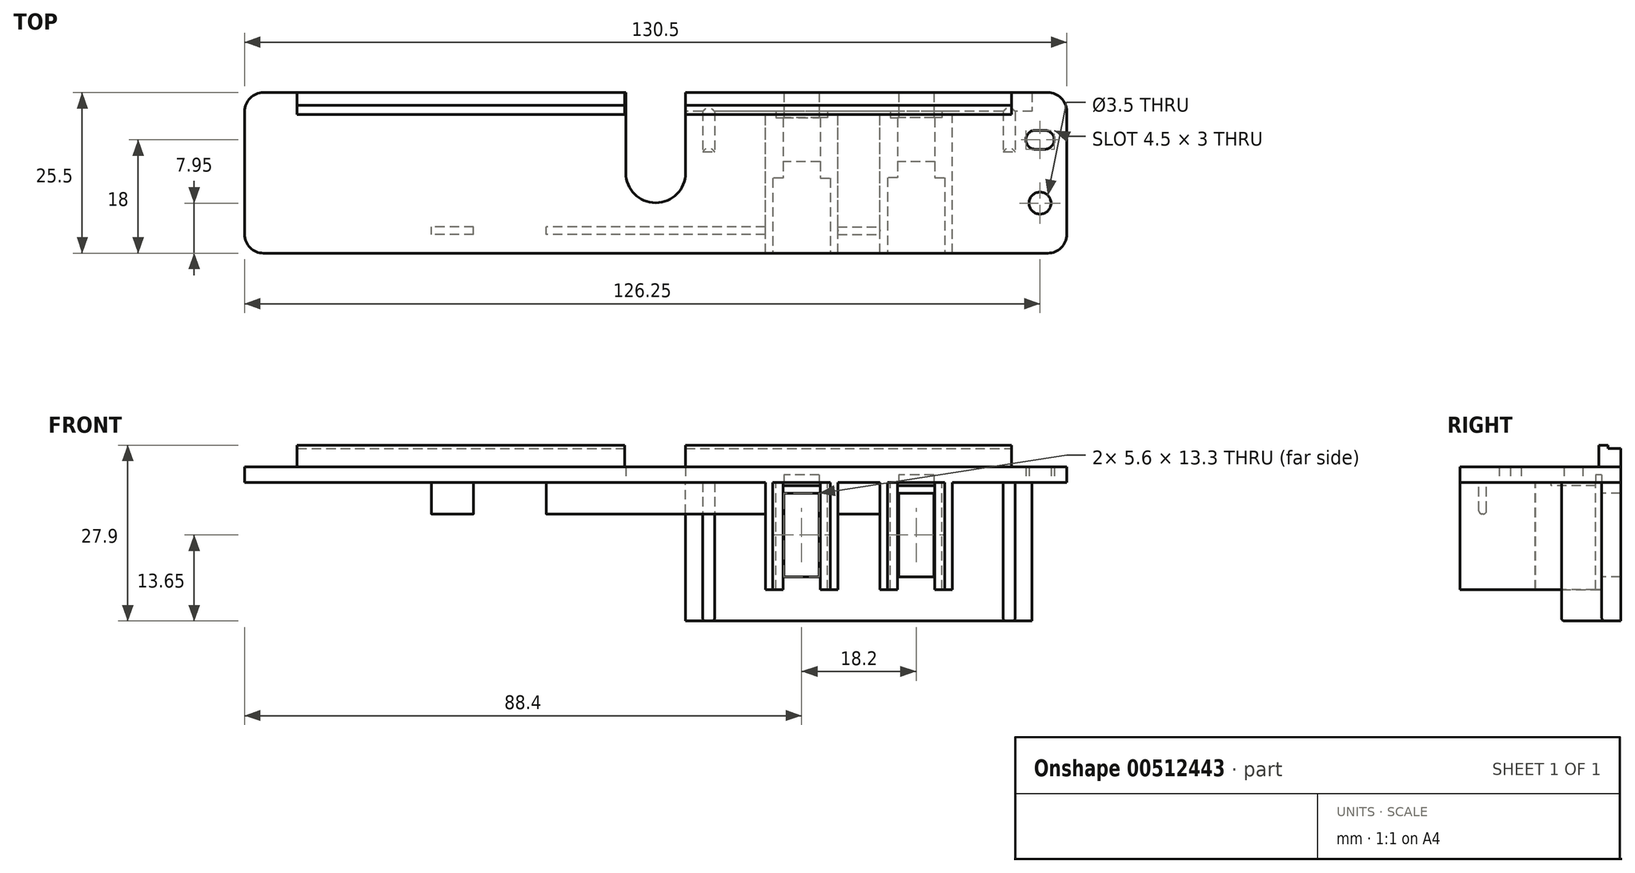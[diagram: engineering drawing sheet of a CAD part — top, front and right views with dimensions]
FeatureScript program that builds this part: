
annotation { "Feature Type Name" : "Feature", "Feature Type Description" : "" }
export const myFeature = defineFeature(function(context is Context, id is Id, definition is map)
    precondition{}
    {
        {
            var Q0;
            Q0=qCreatedBy(makeId("Top.planeOp"),FACE);
            var sketch = newSketch(context, id + "F0", { "sketchPlane" : qUnion([Q0])});
            skLineSegment(sketch, "E0.bottom", {"start": v(65.25, -12.75) * mm, "end": v(-65.25, -12.75) * mm});
            skLineSegment(sketch, "E0.top", {"start": v(65.25, 12.75) * mm, "end": v(-65.25, 12.75) * mm});
            skLineSegment(sketch, "E0.left", {"start": v(65.25, -12.75) * mm, "end": v(65.25, 12.75) * mm});
            skLineSegment(sketch, "E0.right", {"start": v(-65.25, -12.75) * mm, "end": v(-65.25, 12.75) * mm});
            skPoint(sketch, "E0.middle", {"position": v(0, 0) * mm});
            skSolve(sketch);
        }
        {
            var Q0;
            Q0=makeQuery(id+"F0.imprint","IMPRINT",FACE,{"disambiguationData":[TD([[makeQuery(id+"F0.imprint","IMPRINT",EDGE,{"derivedFrom":sQuery(id+"F0.wireOp",EDGE,"E0.bottom")}),-1.0]])]});
            extrude(context, id + "F1", {"entities" : qUnion([Q0]), "depth" : 2.5 * mm});
        }
        {
            var Q0;
            Q0=makeQuery(id+"F1.opExtrude","SWEPT_EDGE",EDGE,{"disambiguationData":[OSD([sQuery(id+"F0.wireOp",EDGE,"E0.top"),sQuery(id+"F0.wireOp",EDGE,"E0.right")])]});
            var Q1;
            Q1=makeQuery(id+"F1.opExtrude","SWEPT_EDGE",EDGE,{"disambiguationData":[OSD([sQuery(id+"F0.wireOp",EDGE,"E0.bottom"),sQuery(id+"F0.wireOp",EDGE,"E0.right")])]});
            var Q2;
            Q2=makeQuery(id+"F1.opExtrude","SWEPT_EDGE",EDGE,{"disambiguationData":[OSD([sQuery(id+"F0.wireOp",EDGE,"E0.top"),sQuery(id+"F0.wireOp",EDGE,"E0.left")])]});
            var Q3;
            Q3=makeQuery(id+"F1.opExtrude","SWEPT_EDGE",EDGE,{"disambiguationData":[OSD([sQuery(id+"F0.wireOp",EDGE,"E0.bottom"),sQuery(id+"F0.wireOp",EDGE,"E0.left")])]});
            fillet(context, id + "F2", {"entities" : qUnion([Q0, Q1, Q2, Q3]), "radius" : 3 * mm, "tangentPropagation" : true, "allowEdgeOverflow" : false});
        }
        {
            var Q0;
            Q0=makeQuery(id+"F1.opExtrude","CAP_FACE",FACE,{"disambiguationData":[OSD([sQuery(id+"F0.wireOp",EDGE,"E0.bottom"),sQuery(id+"F0.wireOp",EDGE,"E0.top"),sQuery(id+"F0.wireOp",EDGE,"E0.left"),sQuery(id+"F0.wireOp",EDGE,"E0.right")])],"isStart":false});
            var sketch = newSketch(context, id + "F3", { "sketchPlane" : qUnion([Q0])});
            skLineSegment(sketch, "E1.bottom", {"start": v(-56.9, 12.75) * mm, "end": v(-4.9, 12.75) * mm});
            skLineSegment(sketch, "E1.top", {"start": v(-56.9, 9.25) * mm, "end": v(-4.9, 9.25) * mm});
            skLineSegment(sketch, "E1.left", {"start": v(-56.9, 12.75) * mm, "end": v(-56.9, 9.25) * mm});
            skLineSegment(sketch, "E1.right", {"start": v(-4.9, 12.75) * mm, "end": v(-4.9, 9.25) * mm});
            skLineSegment(sketch, "E2.bottom", {"start": v(4.5, 12.75) * mm, "end": v(56.5, 12.75) * mm});
            skLineSegment(sketch, "E2.top", {"start": v(4.5, 9.25) * mm, "end": v(56.5, 9.25) * mm});
            skLineSegment(sketch, "E2.left", {"start": v(4.5, 12.75) * mm, "end": v(4.5, 9.25) * mm});
            skLineSegment(sketch, "E2.right", {"start": v(56.5, 12.75) * mm, "end": v(56.5, 9.25) * mm});
            skSolve(sketch);
        }
        {
            var Q0;
            Q0=makeQuery(id+"F3.imprint","IMPRINT",FACE,{"disambiguationData":[TD([[makeQuery(id+"F3.imprint","IMPRINT",EDGE,{"derivedFrom":sQuery(id+"F3.wireOp",EDGE,"E1.bottom")}),1.0]])]});
            var Q1;
            Q1=makeQuery(id+"F3.imprint","IMPRINT",FACE,{"disambiguationData":[TD([[makeQuery(id+"F3.imprint","IMPRINT",EDGE,{"derivedFrom":sQuery(id+"F3.wireOp",EDGE,"E2.bottom")}),1.0]])]});
            extrude(context, id + "F4", {"entities" : qUnion([Q0, Q1]), "operationType" : NewBodyOperationType.ADD, "depth" : 3.4 * mm, "offsetDistance" : 25 * mm});
        }
        {
            var Q0;
            Q0=makeQuery(id+"F1.opExtrude","CAP_FACE",FACE,{"disambiguationData":[OSD([sQuery(id+"F0.wireOp",EDGE,"E0.bottom"),sQuery(id+"F0.wireOp",EDGE,"E0.top"),sQuery(id+"F0.wireOp",EDGE,"E0.left"),sQuery(id+"F0.wireOp",EDGE,"E0.right")])],"isStart":true});
            var sketch = newSketch(context, id + "F5", { "sketchPlane" : qUnion([Q0])});
            skLineSegment(sketch, "E3.bottom", {"start": v(59.75, -12.75) * mm, "end": v(4.75, -12.75) * mm});
            skLineSegment(sketch, "E3.top", {"start": v(59.75, -9.75) * mm, "end": v(4.75, -9.75) * mm});
            skLineSegment(sketch, "E3.left", {"start": v(59.75, -12.75) * mm, "end": v(59.75, -9.75) * mm});
            skLineSegment(sketch, "E3.right", {"start": v(4.75, -12.75) * mm, "end": v(4.75, -9.75) * mm});
            skSolve(sketch);
        }
        {
            var Q0;
            Q0=makeQuery(id+"F5.imprint","IMPRINT",FACE,{"disambiguationData":[TD([[makeQuery(id+"F5.imprint","IMPRINT",EDGE,{"derivedFrom":sQuery(id+"F5.wireOp",EDGE,"E3.bottom")}),-1.0]])]});
            extrude(context, id + "F6", {"entities" : qUnion([Q0]), "operationType" : NewBodyOperationType.ADD, "depth" : 22 * mm, "offsetDistance" : 25 * mm});
        }
        {
            var Q0;
            Q0=makeQuery(id+"F6.opExtrude","CAP_FACE",FACE,{"disambiguationData":[OSD([sQuery(id+"F5.wireOp",EDGE,"E3.bottom"),sQuery(id+"F5.wireOp",EDGE,"E3.top"),sQuery(id+"F5.wireOp",EDGE,"E3.left"),sQuery(id+"F5.wireOp",EDGE,"E3.right")])],"isStart":false});
            var sketch = newSketch(context, id + "F7", { "sketchPlane" : qUnion([Q0])});
            skLineSegment(sketch, "E4.bottom", {"start": v(55.15, -9.75) * mm, "end": v(57.05, -9.75) * mm});
            skLineSegment(sketch, "E4.top", {"start": v(55.15, -3.35) * mm, "end": v(57.05, -3.35) * mm});
            skLineSegment(sketch, "E4.left", {"start": v(55.15, -9.75) * mm, "end": v(55.15, -3.35) * mm});
            skLineSegment(sketch, "E4.right", {"start": v(57.05, -9.75) * mm, "end": v(57.05, -3.35) * mm});
            skSolve(sketch);
        }
        {
            var Q0;
            Q0=makeQuery(id+"F7.imprint","IMPRINT",FACE,{"disambiguationData":[TD([[makeQuery(id+"F7.imprint","IMPRINT",EDGE,{"derivedFrom":sQuery(id+"F7.wireOp",EDGE,"E4.bottom")}),-1.0]])]});
            extrude(context, id + "F8", {"entities" : qUnion([Q0]), "operationType" : NewBodyOperationType.ADD, "endBound" : BoundingType.UP_TO_NEXT, "oppositeDirection" : true, "depth" : 25 * mm, "offsetDistance" : 25 * mm});
        }
        {
            var Q0;
            Q0=makeQuery(id+"F8.boolean.opBoolean","MERGE",FACE,{"derivedFrom":[makeQuery(id+"F6.opExtrude","CAP_FACE",FACE,{"disambiguationData":[OSD([sQuery(id+"F5.wireOp",EDGE,"E3.bottom"),sQuery(id+"F5.wireOp",EDGE,"E3.top"),sQuery(id+"F5.wireOp",EDGE,"E3.left"),sQuery(id+"F5.wireOp",EDGE,"E3.right")])],"isStart":false}),makeQuery(id+"F8.opExtrude","CAP_FACE",FACE,{"disambiguationData":[OSD([sQuery(id+"F7.wireOp",EDGE,"E4.bottom"),sQuery(id+"F7.wireOp",EDGE,"E4.top"),sQuery(id+"F7.wireOp",EDGE,"E4.left"),sQuery(id+"F7.wireOp",EDGE,"E4.right")])],"isStart":true})]});
            var sketch = newSketch(context, id + "F9", { "sketchPlane" : qUnion([Q0])});
            skLineSegment(sketch, "E5.bottom", {"start": v(7.45, -9.75) * mm, "end": v(9.35, -9.75) * mm});
            skLineSegment(sketch, "E5.top", {"start": v(7.45, -3.35) * mm, "end": v(9.35, -3.35) * mm});
            skLineSegment(sketch, "E5.left", {"start": v(7.45, -9.75) * mm, "end": v(7.45, -3.35) * mm});
            skLineSegment(sketch, "E5.right", {"start": v(9.35, -9.75) * mm, "end": v(9.35, -3.35) * mm});
            skSolve(sketch);
        }
        {
            var Q0;
            Q0=makeQuery(id+"F9.imprint","IMPRINT",FACE,{"disambiguationData":[TD([[makeQuery(id+"F9.imprint","IMPRINT",EDGE,{"derivedFrom":sQuery(id+"F9.wireOp",EDGE,"E5.bottom")}),-1.0]])]});
            extrude(context, id + "F10", {"entities" : qUnion([Q0]), "operationType" : NewBodyOperationType.ADD, "endBound" : BoundingType.UP_TO_NEXT, "oppositeDirection" : true, "depth" : 25 * mm, "offsetDistance" : 25 * mm});
        }
        {
            var Q0;
            {var subQ0=sQuery(id+"F0.wireOp",EDGE,"E0.bottom");var subQ1=sQuery(id+"F0.wireOp",EDGE,"E0.left");var subQ2=sQuery(id+"F0.wireOp",EDGE,"E0.top");Q0=makeQuery(id+"FTl0xKzHUKMtFWp_1.boolean.opBoolean","SPLIT",FACE,{"disambiguationData":[TD([makeQuery(id+"F1.opExtrude","SWEPT_FACE",FACE,{"disambiguationData":[OSD([subQ1])]})])],"derivedFrom":makeQuery(id+"F1.opExtrude","CAP_FACE",FACE,{"disambiguationData":[OSD([subQ0,subQ2,subQ1,sQuery(id+"F0.wireOp",EDGE,"E0.right")])],"isStart":true})});}
            var sketch = newSketch(context, id + "F11", { "sketchPlane" : qUnion([Q0])});
            skCircle(sketch, "E6", {"center": v(61, 4.8) * mm, "radius": 1.75 * mm});
            skSolve(sketch);
        }
        {
            var Q0;
            Q0=makeQuery(id+"F11.imprint","IMPRINT",FACE,{"disambiguationData":[TD([[makeQuery(id+"F11.imprint","IMPRINT",EDGE,{"derivedFrom":sQuery(id+"F11.wireOp",EDGE,"E6")}),1.0]])]});
            extrude(context, id + "F12", {"entities" : qUnion([Q0]), "operationType" : NewBodyOperationType.REMOVE, "endBound" : BoundingType.UP_TO_NEXT, "oppositeDirection" : true, "depth" : 25 * mm, "offsetDistance" : 25 * mm});
        }
        {
            var Q0;
            {var subQ0=sQuery(id+"F0.wireOp",EDGE,"E0.bottom");var subQ1=sQuery(id+"F0.wireOp",EDGE,"E0.left");var subQ2=sQuery(id+"F0.wireOp",EDGE,"E0.top");Q0=makeQuery(id+"FTl0xKzHUKMtFWp_1.boolean.opBoolean","SPLIT",FACE,{"disambiguationData":[TD([makeQuery(id+"F1.opExtrude","SWEPT_FACE",FACE,{"disambiguationData":[OSD([subQ1])]})])],"derivedFrom":makeQuery(id+"F1.opExtrude","CAP_FACE",FACE,{"disambiguationData":[OSD([subQ0,subQ2,subQ1,sQuery(id+"F0.wireOp",EDGE,"E0.right")])],"isStart":true})});}
            var sketch = newSketch(context, id + "F13", { "sketchPlane" : qUnion([Q0])});
            skLineSegment(sketch, "E7.bottom", {"start": v(60.25, -3.75) * mm, "end": v(61.75, -3.75) * mm});
            skLineSegment(sketch, "E7.top", {"start": v(60.25, -6.75) * mm, "end": v(61.75, -6.75) * mm});
            skLineSegment(sketch, "E7.left", {"start": v(58.75, -5.25) * mm, "end": v(58.75, -5.25) * mm});
            skLineSegment(sketch, "E7.right", {"start": v(63.25, -5.25) * mm, "end": v(63.25, -5.25) * mm});
            skPoint(sketch, "E8.visualSharp", {"position": v(58.75, -3.75) * mm});
            skArc(sketch, "E8.filletArc", {"start": v(60.25, -3.75) * mm, "mid": v(59.19, -4.19) * mm, "end": v(58.75, -5.25) * mm});
            skPoint(sketch, "E9.visualSharp", {"position": v(58.75, -6.75) * mm});
            skArc(sketch, "E9.filletArc", {"start": v(58.75, -5.25) * mm, "mid": v(59.19, -6.31) * mm, "end": v(60.25, -6.75) * mm});
            skPoint(sketch, "E10.visualSharp", {"position": v(63.25, -6.75) * mm});
            skArc(sketch, "E10.filletArc", {"start": v(61.75, -6.75) * mm, "mid": v(62.81, -6.31) * mm, "end": v(63.25, -5.25) * mm});
            skPoint(sketch, "E11.visualSharp", {"position": v(63.25, -3.75) * mm});
            skArc(sketch, "E11.filletArc", {"start": v(63.25, -5.25) * mm, "mid": v(62.81, -4.19) * mm, "end": v(61.75, -3.75) * mm});
            skSolve(sketch);
        }
        {
            var Q0;
            Q0=makeQuery(id+"F13.imprint","IMPRINT",FACE,{"disambiguationData":[TD([[makeQuery(id+"F13.imprint","IMPRINT",EDGE,{"derivedFrom":sQuery(id+"F13.wireOp",EDGE,"E7.bottom")}),-1.0]])]});
            extrude(context, id + "F14", {"entities" : qUnion([Q0]), "operationType" : NewBodyOperationType.REMOVE, "endBound" : BoundingType.UP_TO_NEXT, "oppositeDirection" : true, "depth" : 25 * mm, "offsetDistance" : 25 * mm});
        }
        {
            var Q0;
            Q0=makeQuery(id+"F4.opExtrude","SWEPT_FACE",FACE,{"disambiguationData":[OSD([sQuery(id+"F3.wireOp",EDGE,"E2.right")])]});
            var sketch = newSketch(context, id + "F15", { "sketchPlane" : qUnion([Q0])});
            skLineSegment(sketch, "E12.bottom", {"start": v(12.75, 5.9) * mm, "end": v(10.75, 5.9) * mm});
            skLineSegment(sketch, "E12.top", {"start": v(12.75, 5.4) * mm, "end": v(10.75, 5.4) * mm});
            skLineSegment(sketch, "E12.left", {"start": v(12.75, 5.9) * mm, "end": v(12.75, 5.4) * mm});
            skLineSegment(sketch, "E12.right", {"start": v(10.75, 5.9) * mm, "end": v(10.75, 5.4) * mm});
            skSolve(sketch);
        }
        {
            var Q0;
            Q0=makeQuery(id+"F15.imprint","IMPRINT",FACE,{"disambiguationData":[TD([[makeQuery(id+"F15.imprint","IMPRINT",EDGE,{"derivedFrom":sQuery(id+"F15.wireOp",EDGE,"E12.bottom")}),1.0]])]});
            extrude(context, id + "F16", {"entities" : qUnion([Q0]), "operationType" : NewBodyOperationType.REMOVE, "endBound" : BoundingType.THROUGH_ALL, "oppositeDirection" : true, "depth" : 25 * mm, "offsetDistance" : 25 * mm});
        }
        {
            var Q0;
            {var subQ0=sQuery(id+"F7.wireOp",EDGE,"E4.left");var subQ2=sQuery(id+"F5.wireOp",EDGE,"E3.right");var subQ3=sQuery(id+"F5.wireOp",EDGE,"E3.top");var subQ6=makeQuery(id+"F8.opExtrude","SWEPT_FACE",FACE,{"disambiguationData":[OSD([subQ0])]});Q0=makeQuery(id+"F10.boolean.opBoolean","SPLIT",FACE,{"disambiguationData":[TD([subQ6])],"derivedFrom":makeQuery(id+"F8.boolean.opBoolean","SPLIT",FACE,{"disambiguationData":[TD([makeQuery(id+"F6.opExtrude","SWEPT_FACE",FACE,{"disambiguationData":[OSD([subQ2])]})])],"derivedFrom":makeQuery(id+"F6.opExtrude","SWEPT_FACE",FACE,{"disambiguationData":[OSD([subQ3])]})})});}
            var sketch = newSketch(context, id + "F17", { "sketchPlane" : qUnion([Q0])});
            skLineSegment(sketch, "E13.bottom", {"start": v(44.15, -1.7) * mm, "end": v(38.55, -1.7) * mm});
            skLineSegment(sketch, "E13.top", {"start": v(44.15, -15) * mm, "end": v(38.55, -15) * mm});
            skLineSegment(sketch, "E13.left", {"start": v(44.15, -1.7) * mm, "end": v(44.15, -15) * mm});
            skLineSegment(sketch, "E13.right", {"start": v(38.55, -1.7) * mm, "end": v(38.55, -15) * mm});
            skLineSegment(sketch, "E14.bottom", {"start": v(25.95, -1.7) * mm, "end": v(20.35, -1.7) * mm});
            skLineSegment(sketch, "E14.top", {"start": v(25.95, -15) * mm, "end": v(20.35, -15) * mm});
            skLineSegment(sketch, "E14.left", {"start": v(25.95, -1.7) * mm, "end": v(25.95, -15) * mm});
            skLineSegment(sketch, "E14.right", {"start": v(20.35, -1.7) * mm, "end": v(20.35, -15) * mm});
            skSolve(sketch);
        }
        {
            var Q0;
            Q0=makeQuery(id+"F17.imprint","IMPRINT",FACE,{"disambiguationData":[TD([[makeQuery(id+"F17.imprint","IMPRINT",EDGE,{"derivedFrom":sQuery(id+"F17.wireOp",EDGE,"E13.bottom")}),1.0]])]});
            var Q1;
            Q1=makeQuery(id+"F17.imprint","IMPRINT",FACE,{"disambiguationData":[TD([[makeQuery(id+"F17.imprint","IMPRINT",EDGE,{"derivedFrom":sQuery(id+"F17.wireOp",EDGE,"E14.bottom")}),1.0]])]});
            extrude(context, id + "F18", {"entities" : qUnion([Q0, Q1]), "operationType" : NewBodyOperationType.REMOVE, "endBound" : BoundingType.THROUGH_ALL, "oppositeDirection" : true, "depth" : 25 * mm, "offsetDistance" : 25 * mm});
        }
        {
            var Q0;
            Q0=makeQuery(id+"F1.opExtrude","CAP_FACE",FACE,{"disambiguationData":[OSD([sQuery(id+"F0.wireOp",EDGE,"E0.bottom"),sQuery(id+"F0.wireOp",EDGE,"E0.top"),sQuery(id+"F0.wireOp",EDGE,"E0.left"),sQuery(id+"F0.wireOp",EDGE,"E0.right")])],"isStart":true});
            var sketch = newSketch(context, id + "F19", { "sketchPlane" : qUnion([Q0])});
            skLineSegment(sketch, "E15.bottom", {"start": v(44.15, -9.75) * mm, "end": v(38.55, -9.75) * mm});
            skLineSegment(sketch, "E15.top", {"start": v(44.15, -8.75) * mm, "end": v(38.55, -8.75) * mm});
            skLineSegment(sketch, "E15.left", {"start": v(44.15, -9.75) * mm, "end": v(44.15, -8.75) * mm});
            skLineSegment(sketch, "E15.right", {"start": v(38.55, -9.75) * mm, "end": v(38.55, -8.75) * mm});
            skLineSegment(sketch, "E16.bottom", {"start": v(20.35, -9.75) * mm, "end": v(25.95, -9.75) * mm});
            skLineSegment(sketch, "E16.top", {"start": v(20.35, -8.75) * mm, "end": v(25.95, -8.75) * mm});
            skLineSegment(sketch, "E16.left", {"start": v(20.35, -9.75) * mm, "end": v(20.35, -8.75) * mm});
            skLineSegment(sketch, "E16.right", {"start": v(25.95, -9.75) * mm, "end": v(25.95, -8.75) * mm});
            skSolve(sketch);
        }
        {
            var Q0;
            Q0=makeQuery(id+"F19.imprint","IMPRINT",FACE,{"disambiguationData":[TD([[makeQuery(id+"F19.imprint","IMPRINT",EDGE,{"derivedFrom":sQuery(id+"F19.wireOp",EDGE,"E15.bottom")}),-1.0]])]});
            var Q1;
            Q1=makeQuery(id+"F19.imprint","IMPRINT",FACE,{"disambiguationData":[TD([[makeQuery(id+"F19.imprint","IMPRINT",EDGE,{"derivedFrom":sQuery(id+"F19.wireOp",EDGE,"E16.bottom")}),-1.0]])]});
            extrude(context, id + "F20", {"entities" : qUnion([Q0, Q1]), "operationType" : NewBodyOperationType.REMOVE, "oppositeDirection" : true, "depth" : 1.2 * mm, "offsetDistance" : 25 * mm});
        }
        {
            var Q0;
            Q0=makeQuery(id+"F1.opExtrude","CAP_FACE",FACE,{"disambiguationData":[OSD([sQuery(id+"F0.wireOp",EDGE,"E0.bottom"),sQuery(id+"F0.wireOp",EDGE,"E0.top"),sQuery(id+"F0.wireOp",EDGE,"E0.left"),sQuery(id+"F0.wireOp",EDGE,"E0.right")])],"isStart":true});
            var sketch = newSketch(context, id + "F21", { "sketchPlane" : qUnion([Q0])});
            skLineSegment(sketch, "E17", {"start": v(45.45, -9.75) * mm, "end": v(45.45, -8.75) * mm});
            skLineSegment(sketch, "E18", {"start": v(45.45, -8.75) * mm, "end": v(44.3, -8.75) * mm});
            skLineSegment(sketch, "E19", {"start": v(44.3, -8.75) * mm, "end": v(44.3, 0.75) * mm});
            skLineSegment(sketch, "E20", {"start": v(44.3, 0.75) * mm, "end": v(45.9, 0.75) * mm});
            skLineSegment(sketch, "E21", {"start": v(45.9, 0.75) * mm, "end": v(45.9, 12.75) * mm});
            skLineSegment(sketch, "E22", {"start": v(45.9, 12.75) * mm, "end": v(47.1, 12.75) * mm});
            skLineSegment(sketch, "E23", {"start": v(47.1, 12.75) * mm, "end": v(47.1, -9.75) * mm});
            skLineSegment(sketch, "E24", {"start": v(47.1, -9.75) * mm, "end": v(45.45, -9.75) * mm});
            skLineSegment(sketch, "E25", {"start": v(37.25, -9.75) * mm, "end": v(37.25, -8.75) * mm});
            skLineSegment(sketch, "E26", {"start": v(37.25, -8.75) * mm, "end": v(38.4, -8.75) * mm});
            skLineSegment(sketch, "E27", {"start": v(38.4, -8.75) * mm, "end": v(38.4, 0.75) * mm});
            skLineSegment(sketch, "E28", {"start": v(38.4, 0.75) * mm, "end": v(36.8, 0.75) * mm});
            skLineSegment(sketch, "E29", {"start": v(36.8, 0.75) * mm, "end": v(36.8, 12.75) * mm});
            skLineSegment(sketch, "E30", {"start": v(36.8, 12.75) * mm, "end": v(35.6, 12.75) * mm});
            skLineSegment(sketch, "E31", {"start": v(35.6, 12.75) * mm, "end": v(35.6, -9.75) * mm});
            skLineSegment(sketch, "E32", {"start": v(35.6, -9.75) * mm, "end": v(37.25, -9.75) * mm});
            skLineSegment(sketch, "E33", {"start": v(28.9, 12.75) * mm, "end": v(28.9, -9.75) * mm});
            skLineSegment(sketch, "E34", {"start": v(28.9, -9.75) * mm, "end": v(27.25, -9.75) * mm});
            skLineSegment(sketch, "E35", {"start": v(27.25, -9.75) * mm, "end": v(27.25, -8.75) * mm});
            skLineSegment(sketch, "E36", {"start": v(27.25, -8.75) * mm, "end": v(26.1, -8.75) * mm});
            skLineSegment(sketch, "E37", {"start": v(26.1, -8.75) * mm, "end": v(26.1, 0.85) * mm});
            skLineSegment(sketch, "E38", {"start": v(26.1, 0.85) * mm, "end": v(27.7, 0.85) * mm});
            skLineSegment(sketch, "E39", {"start": v(27.7, 0.85) * mm, "end": v(27.7, 12.75) * mm});
            skLineSegment(sketch, "E40", {"start": v(27.7, 12.75) * mm, "end": v(28.9, 12.75) * mm});
            skLineSegment(sketch, "E41", {"start": v(19.05, -9.75) * mm, "end": v(19.05, -8.75) * mm});
            skLineSegment(sketch, "E42", {"start": v(19.05, -8.75) * mm, "end": v(20.2, -8.75) * mm});
            skLineSegment(sketch, "E43", {"start": v(20.2, -8.75) * mm, "end": v(20.2, 0.85) * mm});
            skLineSegment(sketch, "E44", {"start": v(20.2, 0.85) * mm, "end": v(18.6, 0.85) * mm});
            skLineSegment(sketch, "E45", {"start": v(18.6, 0.85) * mm, "end": v(18.6, 12.75) * mm});
            skLineSegment(sketch, "E46", {"start": v(18.6, 12.75) * mm, "end": v(17.4, 12.75) * mm});
            skLineSegment(sketch, "E47", {"start": v(17.4, 12.75) * mm, "end": v(17.4, -9.75) * mm});
            skLineSegment(sketch, "E48", {"start": v(17.4, -9.75) * mm, "end": v(19.05, -9.75) * mm});
            skSolve(sketch);
        }
        {
            var Q0;
            Q0=makeQuery(id+"F21.imprint","IMPRINT",FACE,{"disambiguationData":[TD([[makeQuery(id+"F21.imprint","IMPRINT",EDGE,{"derivedFrom":sQuery(id+"F21.wireOp",EDGE,"E17")}),-1.0]])]});
            var Q1;
            Q1=makeQuery(id+"F21.imprint","IMPRINT",FACE,{"disambiguationData":[TD([[makeQuery(id+"F21.imprint","IMPRINT",EDGE,{"derivedFrom":sQuery(id+"F21.wireOp",EDGE,"E25")}),1.0]])]});
            var Q2;
            Q2=makeQuery(id+"F21.imprint","IMPRINT",FACE,{"disambiguationData":[TD([[makeQuery(id+"F21.imprint","IMPRINT",EDGE,{"derivedFrom":sQuery(id+"F21.wireOp",EDGE,"E33")}),-1.0]])]});
            var Q3;
            Q3=makeQuery(id+"F21.imprint","IMPRINT",FACE,{"disambiguationData":[TD([[makeQuery(id+"F21.imprint","IMPRINT",EDGE,{"derivedFrom":sQuery(id+"F21.wireOp",EDGE,"E41")}),1.0]])]});
            extrude(context, id + "F22", {"entities" : qUnion([Q0, Q1, Q2, Q3]), "operationType" : NewBodyOperationType.ADD, "depth" : 17 * mm, "offsetDistance" : 25 * mm});
        }
        {
            var Q0;
            {var subQ12=sQuery(id+"F5.wireOp",EDGE,"E3.top");var subQ25=sQuery(id+"F0.wireOp",EDGE,"E0.bottom");var subQ27=sQuery(id+"F0.wireOp",EDGE,"E0.top");var subQ35=makeQuery(id+"F6.opExtrude","SWEPT_FACE",FACE,{"disambiguationData":[OSD([subQ12])]});var subQ38=sQuery(id+"F0.wireOp",EDGE,"E0.right");Q0=makeQuery(id+"F36xmBUTzq5bmo9_1.1.F22.boolean.opBoolean","SPLIT",FACE,{"disambiguationData":[TD([subQ35])],"derivedFrom":makeQuery(id+"F22.boolean.opBoolean","SPLIT",FACE,{"disambiguationData":[TD([makeQuery(id+"F1.opExtrude","SWEPT_FACE",FACE,{"disambiguationData":[OSD([subQ38])]})])],"derivedFrom":makeQuery(id+"F1.opExtrude","CAP_FACE",FACE,{"disambiguationData":[OSD([subQ25,subQ27,sQuery(id+"F0.wireOp",EDGE,"E0.left"),subQ38])],"isStart":true})})});}
            var sketch = newSketch(context, id + "F23", { "sketchPlane" : qUnion([Q0])});
            skLineSegment(sketch, "E49.bottom", {"start": v(-4.75, -12.75) * mm, "end": v(4.75, -12.75) * mm});
            skLineSegment(sketch, "E49.top", {"start": v(-4.75, 0) * mm, "end": v(4.75, 0) * mm});
            skLineSegment(sketch, "E49.left", {"start": v(-4.75, -12.75) * mm, "end": v(-4.75, 0) * mm});
            skLineSegment(sketch, "E49.right", {"start": v(4.75, -12.75) * mm, "end": v(4.75, 0) * mm});
            skCircle(sketch, "E50", {"center": v(0, 0) * mm, "radius": 4.75 * mm});
            skSolve(sketch);
        }
        {
            var Q0;
            {var subQ0=sQuery(id+"F23.wireOp",EDGE,"E49.top");Q0=makeQuery(id+"F23.imprint","IMPRINT",FACE,{"disambiguationData":[TD([[makeQuery(id+"F23.imprint","IMPRINT",EDGE,{"derivedFrom":subQ0}),1.0]])]});}
            var Q1;
            {var subQ0=sQuery(id+"F23.wireOp",EDGE,"E49.top");Q1=makeQuery(id+"F23.imprint","IMPRINT",FACE,{"disambiguationData":[TD([[makeQuery(id+"F23.imprint","IMPRINT",EDGE,{"derivedFrom":subQ0}),-1.0]])]});}
            var Q2;
            {var subQ13=sQuery(id+"F23.wireOp",EDGE,"E49.bottom");Q2=makeQuery(id+"F23.imprint","IMPRINT",FACE,{"disambiguationData":[TD([[makeQuery(id+"F23.imprint","IMPRINT",EDGE,{"derivedFrom":subQ13}),-1.0]])]});}
            extrude(context, id + "F24", {"entities" : qUnion([Q0, Q1, Q2]), "operationType" : NewBodyOperationType.REMOVE, "endBound" : BoundingType.THROUGH_ALL, "oppositeDirection" : true, "depth" : 25 * mm, "offsetDistance" : 25 * mm});
        }
        {
            var Q0;
            {var subQ12=sQuery(id+"F5.wireOp",EDGE,"E3.top");var subQ25=sQuery(id+"F0.wireOp",EDGE,"E0.bottom");var subQ27=sQuery(id+"F0.wireOp",EDGE,"E0.top");var subQ35=makeQuery(id+"F6.opExtrude","SWEPT_FACE",FACE,{"disambiguationData":[OSD([subQ12])]});var subQ38=sQuery(id+"F0.wireOp",EDGE,"E0.right");Q0=makeQuery(id+"F36xmBUTzq5bmo9_1.1.F22.boolean.opBoolean","SPLIT",FACE,{"disambiguationData":[TD([subQ35])],"derivedFrom":makeQuery(id+"F22.boolean.opBoolean","SPLIT",FACE,{"disambiguationData":[TD([makeQuery(id+"F1.opExtrude","SWEPT_FACE",FACE,{"disambiguationData":[OSD([subQ38])]})])],"derivedFrom":makeQuery(id+"F1.opExtrude","CAP_FACE",FACE,{"disambiguationData":[OSD([subQ25,subQ27,sQuery(id+"F0.wireOp",EDGE,"E0.left"),subQ38])],"isStart":true})})});}
            var sketch = newSketch(context, id + "F25", { "sketchPlane" : qUnion([Q0])});
            skLineSegment(sketch, "E51.bottom", {"start": v(17.4, 9.75) * mm, "end": v(-17.4, 9.75) * mm});
            skLineSegment(sketch, "E51.top", {"start": v(17.4, 8.55) * mm, "end": v(-17.4, 8.55) * mm});
            skLineSegment(sketch, "E51.left", {"start": v(17.4, 9.75) * mm, "end": v(17.4, 8.55) * mm});
            skLineSegment(sketch, "E51.right", {"start": v(-17.4, 9.75) * mm, "end": v(-17.4, 8.55) * mm});
            skLineSegment(sketch, "E52.bottom", {"start": v(28.9, 8.55) * mm, "end": v(35.6, 8.55) * mm});
            skLineSegment(sketch, "E52.top", {"start": v(28.9, 9.75) * mm, "end": v(35.6, 9.75) * mm});
            skLineSegment(sketch, "E52.left", {"start": v(28.9, 8.55) * mm, "end": v(28.9, 9.75) * mm});
            skLineSegment(sketch, "E52.right", {"start": v(35.6, 8.55) * mm, "end": v(35.6, 9.75) * mm});
            skLineSegment(sketch, "E53.bottom", {"start": v(-28.9, 9.75) * mm, "end": v(-35.6, 9.75) * mm});
            skLineSegment(sketch, "E53.top", {"start": v(-28.9, 8.55) * mm, "end": v(-35.6, 8.55) * mm});
            skLineSegment(sketch, "E53.left", {"start": v(-28.9, 9.75) * mm, "end": v(-28.9, 8.55) * mm});
            skLineSegment(sketch, "E53.right", {"start": v(-35.6, 9.75) * mm, "end": v(-35.6, 8.55) * mm});
            skSolve(sketch);
        }
        {
            var Q0;
            Q0=makeQuery(id+"F25.imprint","IMPRINT",FACE,{"disambiguationData":[TD([[makeQuery(id+"F25.imprint","IMPRINT",EDGE,{"derivedFrom":sQuery(id+"F25.wireOp",EDGE,"E52.bottom")}),1.0]])]});
            var Q1;
            Q1=makeQuery(id+"F25.imprint","IMPRINT",FACE,{"disambiguationData":[TD([[makeQuery(id+"F25.imprint","IMPRINT",EDGE,{"derivedFrom":sQuery(id+"F25.wireOp",EDGE,"E51.bottom")}),1.0]])]});
            var Q2;
            Q2=makeQuery(id+"F25.imprint","IMPRINT",FACE,{"disambiguationData":[TD([[makeQuery(id+"F25.imprint","IMPRINT",EDGE,{"derivedFrom":sQuery(id+"F25.wireOp",EDGE,"E53.bottom")}),1.0]])]});
            extrude(context, id + "F26", {"entities" : qUnion([Q0, Q1, Q2]), "operationType" : NewBodyOperationType.ADD, "depth" : 5 * mm, "offsetDistance" : 25 * mm});
        }
        {
            var Q0;
            {var subQ0=sQuery(id+"F7.wireOp",EDGE,"E4.left");var subQ2=makeQuery(id+"F8.opExtrude","SWEPT_FACE",FACE,{"disambiguationData":[OSD([subQ0])]});var subQ3=sQuery(id+"F5.wireOp",EDGE,"E3.top");var subQ5=sQuery(id+"F5.wireOp",EDGE,"E3.right");Q0=makeQuery(id+"F10.boolean.opBoolean","SPLIT",EDGE,{"disambiguationData":[TD([subQ2])],"derivedFrom":makeQuery(id+"F8.boolean.opBoolean","SPLIT",EDGE,{"disambiguationData":[TD([makeQuery(id+"F6.opExtrude","SWEPT_FACE",FACE,{"disambiguationData":[OSD([subQ5])]})])],"derivedFrom":makeQuery(id+"F6.opExtrude","CAP_EDGE",EDGE,{"disambiguationData":[OSD([subQ3])],"isStart":false})})});}
            var Q1;
            {var subQ0=sQuery(id+"F7.wireOp",EDGE,"E4.left");var subQ1=makeQuery(id+"FbdN5aHEnnnu9Vr_1.1.F8.opExtrude","SWEPT_FACE",FACE,{"disambiguationData":[OSD([subQ0])]});var subQ4=sQuery(id+"F5.wireOp",EDGE,"E3.top");var subQ6=sQuery(id+"F5.wireOp",EDGE,"E3.right");Q1=makeQuery(id+"FbdN5aHEnnnu9Vr_1.1.F10.boolean.opBoolean","SPLIT",EDGE,{"disambiguationData":[TD([subQ1])],"derivedFrom":makeQuery(id+"FbdN5aHEnnnu9Vr_1.1.F8.boolean.opBoolean","SPLIT",EDGE,{"disambiguationData":[TD([makeQuery(id+"FbdN5aHEnnnu9Vr_1.1.F6.opExtrude","SWEPT_FACE",FACE,{"disambiguationData":[OSD([subQ6])]})])],"derivedFrom":makeQuery(id+"FbdN5aHEnnnu9Vr_1.1.F6.opExtrude","CAP_EDGE",EDGE,{"disambiguationData":[OSD([subQ4])],"isStart":false})})});}
            var Q2;
            Q2=makeQuery(id+"F8.opExtrude","CAP_EDGE",EDGE,{"disambiguationData":[OSD([sQuery(id+"F7.wireOp",EDGE,"E4.left")])],"isStart":true});
            var Q3;
            Q3=makeQuery(id+"F8.opExtrude","CAP_EDGE",EDGE,{"disambiguationData":[OSD([sQuery(id+"F7.wireOp",EDGE,"E4.right")])],"isStart":true});
            var Q4;
            Q4=makeQuery(id+"F8.opExtrude","CAP_EDGE",EDGE,{"disambiguationData":[OSD([sQuery(id+"F7.wireOp",EDGE,"E4.top")])],"isStart":true});
            var Q5;
            {var subQ1=sQuery(id+"F5.wireOp",EDGE,"E3.left");var subQ2=sQuery(id+"F5.wireOp",EDGE,"E3.top");Q5=makeQuery(id+"F8.boolean.opBoolean","SPLIT",EDGE,{"disambiguationData":[TD([makeQuery(id+"F6.opExtrude","SWEPT_FACE",FACE,{"disambiguationData":[OSD([subQ1])]})])],"derivedFrom":makeQuery(id+"F6.opExtrude","CAP_EDGE",EDGE,{"disambiguationData":[OSD([subQ2])],"isStart":false})});}
            var Q6;
            Q6=makeQuery(id+"F10.opExtrude","CAP_EDGE",EDGE,{"disambiguationData":[OSD([sQuery(id+"F9.wireOp",EDGE,"E5.right")])],"isStart":true});
            var Q7;
            Q7=makeQuery(id+"F10.opExtrude","CAP_EDGE",EDGE,{"disambiguationData":[OSD([sQuery(id+"F9.wireOp",EDGE,"E5.left")])],"isStart":true});
            var Q8;
            Q8=makeQuery(id+"F10.opExtrude","CAP_EDGE",EDGE,{"disambiguationData":[OSD([sQuery(id+"F9.wireOp",EDGE,"E5.top")])],"isStart":true});
            var Q9;
            {var subQ2=sQuery(id+"F5.wireOp",EDGE,"E3.right");var subQ3=makeQuery(id+"F6.opExtrude","SWEPT_FACE",FACE,{"disambiguationData":[OSD([subQ2])]});var subQ4=sQuery(id+"F5.wireOp",EDGE,"E3.top");Q9=makeQuery(id+"F10.boolean.opBoolean","SPLIT",EDGE,{"disambiguationData":[TD([subQ3])],"derivedFrom":makeQuery(id+"F8.boolean.opBoolean","SPLIT",EDGE,{"disambiguationData":[TD([subQ3])],"derivedFrom":makeQuery(id+"F6.opExtrude","CAP_EDGE",EDGE,{"disambiguationData":[OSD([subQ4])],"isStart":false})})});}
            var Q10;
            {var subQ0=sQuery(id+"F5.wireOp",EDGE,"E3.right");var subQ1=makeQuery(id+"FbdN5aHEnnnu9Vr_1.1.F6.opExtrude","SWEPT_FACE",FACE,{"disambiguationData":[OSD([subQ0])]});var subQ4=sQuery(id+"F5.wireOp",EDGE,"E3.top");Q10=makeQuery(id+"FbdN5aHEnnnu9Vr_1.1.F10.boolean.opBoolean","SPLIT",EDGE,{"disambiguationData":[TD([subQ1])],"derivedFrom":makeQuery(id+"FbdN5aHEnnnu9Vr_1.1.F8.boolean.opBoolean","SPLIT",EDGE,{"disambiguationData":[TD([subQ1])],"derivedFrom":makeQuery(id+"FbdN5aHEnnnu9Vr_1.1.F6.opExtrude","CAP_EDGE",EDGE,{"disambiguationData":[OSD([subQ4])],"isStart":false})})});}
            var Q11;
            Q11=makeQuery(id+"FbdN5aHEnnnu9Vr_1.1.F10.opExtrude","CAP_EDGE",EDGE,{"disambiguationData":[OSD([sQuery(id+"F9.wireOp",EDGE,"E5.left")])],"isStart":true});
            var Q12;
            Q12=makeQuery(id+"FbdN5aHEnnnu9Vr_1.1.F10.opExtrude","CAP_EDGE",EDGE,{"disambiguationData":[OSD([sQuery(id+"F9.wireOp",EDGE,"E5.right")])],"isStart":true});
            var Q13;
            Q13=makeQuery(id+"FbdN5aHEnnnu9Vr_1.1.F10.opExtrude","CAP_EDGE",EDGE,{"disambiguationData":[OSD([sQuery(id+"F9.wireOp",EDGE,"E5.top")])],"isStart":true});
            var Q14;
            Q14=makeQuery(id+"FbdN5aHEnnnu9Vr_1.1.F8.opExtrude","CAP_EDGE",EDGE,{"disambiguationData":[OSD([sQuery(id+"F7.wireOp",EDGE,"E4.left")])],"isStart":true});
            var Q15;
            Q15=makeQuery(id+"FbdN5aHEnnnu9Vr_1.1.F8.opExtrude","CAP_EDGE",EDGE,{"disambiguationData":[OSD([sQuery(id+"F7.wireOp",EDGE,"E4.top")])],"isStart":true});
            var Q16;
            Q16=makeQuery(id+"FbdN5aHEnnnu9Vr_1.1.F8.opExtrude","CAP_EDGE",EDGE,{"disambiguationData":[OSD([sQuery(id+"F7.wireOp",EDGE,"E4.right")])],"isStart":true});
            var Q17;
            {var subQ0=sQuery(id+"F5.wireOp",EDGE,"E3.left");var subQ2=sQuery(id+"F5.wireOp",EDGE,"E3.top");Q17=makeQuery(id+"FbdN5aHEnnnu9Vr_1.1.F8.boolean.opBoolean","SPLIT",EDGE,{"disambiguationData":[TD([makeQuery(id+"FbdN5aHEnnnu9Vr_1.1.F6.opExtrude","SWEPT_FACE",FACE,{"disambiguationData":[OSD([subQ0])]})])],"derivedFrom":makeQuery(id+"FbdN5aHEnnnu9Vr_1.1.F6.opExtrude","CAP_EDGE",EDGE,{"disambiguationData":[OSD([subQ2])],"isStart":false})});}
            var Q18;
            Q18=makeQuery(id+"F26.opExtrude","CAP_EDGE",EDGE,{"disambiguationData":[OSD([sQuery(id+"F25.wireOp",EDGE,"E51.bottom")])],"isStart":false});
            var Q19;
            Q19=makeQuery(id+"F26.opExtrude","CAP_EDGE",EDGE,{"disambiguationData":[OSD([sQuery(id+"F25.wireOp",EDGE,"E52.top")])],"isStart":false});
            var Q20;
            Q20=makeQuery(id+"F26.opExtrude","CAP_EDGE",EDGE,{"disambiguationData":[OSD([sQuery(id+"F25.wireOp",EDGE,"E52.bottom")])],"isStart":false});
            var Q21;
            Q21=makeQuery(id+"F26.opExtrude","CAP_EDGE",EDGE,{"disambiguationData":[OSD([sQuery(id+"F25.wireOp",EDGE,"E51.top")])],"isStart":false});
            var Q22;
            Q22=makeQuery(id+"F26.opExtrude","CAP_EDGE",EDGE,{"disambiguationData":[OSD([sQuery(id+"F25.wireOp",EDGE,"E53.top")])],"isStart":false});
            var Q23;
            Q23=makeQuery(id+"F26.opExtrude","CAP_EDGE",EDGE,{"disambiguationData":[OSD([sQuery(id+"F25.wireOp",EDGE,"E53.bottom")])],"isStart":false});
            fillet(context, id + "F27", {"entities" : qUnion([Q0, Q1, Q2, Q3, Q4, Q5, Q6, Q7, Q8, Q9, Q10, Q11, Q12, Q13, Q14, Q15, Q16, Q17, Q18, Q19, Q20, Q21, Q22, Q23]), "radius" : 0.5 * mm, "tangentPropagation" : true, "allowEdgeOverflow" : false});
        }
        {
            var Q0;
            {var subQ0=sQuery(id+"F0.wireOp",EDGE,"E0.bottom");Q0=makeQuery(id+"F22.boolean.opBoolean","SPLIT",FACE,{"disambiguationData":[TD([makeQuery(id+"F20.boolean.opBoolean","COPY",FACE,{"derivedFrom":makeQuery(id+"F20.opExtrude","SWEPT_FACE",FACE,{"disambiguationData":[OSD([sQuery(id+"F19.wireOp",EDGE,"E15.top")])]})})])],"derivedFrom":makeQuery(id+"F1.opExtrude","CAP_FACE",FACE,{"disambiguationData":[OSD([subQ0,sQuery(id+"F0.wireOp",EDGE,"E0.top"),sQuery(id+"F0.wireOp",EDGE,"E0.left"),sQuery(id+"F0.wireOp",EDGE,"E0.right")])],"isStart":true})});}
            var sketch = newSketch(context, id + "F28", { "sketchPlane" : qUnion([Q0])});
            skLineSegment(sketch, "E54.bottom", {"start": v(44.3, -8.75) * mm, "end": v(38.4, -8.75) * mm});
            skLineSegment(sketch, "E54.top", {"start": v(44.3, -1.75) * mm, "end": v(38.4, -1.75) * mm});
            skLineSegment(sketch, "E54.left", {"start": v(44.3, -8.75) * mm, "end": v(44.3, -1.75) * mm});
            skLineSegment(sketch, "E54.right", {"start": v(38.4, -8.75) * mm, "end": v(38.4, -1.75) * mm});
            skPoint(sketch, "E55.firstSnap0", {"position": v(37.83, -8.75) * mm});
            skLineSegment(sketch, "E55.bottom", {"start": v(26.1, -8.75) * mm, "end": v(20.2, -8.75) * mm});
            skLineSegment(sketch, "E55.top", {"start": v(26.1, -1.75) * mm, "end": v(20.2, -1.75) * mm});
            skLineSegment(sketch, "E55.left", {"start": v(26.1, -8.75) * mm, "end": v(26.1, -1.75) * mm});
            skLineSegment(sketch, "E55.right", {"start": v(20.2, -8.75) * mm, "end": v(20.2, -1.75) * mm});
            skSolve(sketch);
        }
        {
            var Q0;
            Q0 = qSketchRegion(id + "F28", true);
            extrude(context, id + "F29", {"entities" : qUnion([Q0]), "operationType" : NewBodyOperationType.ADD, "depth" : 0.5 * mm, "offsetDistance" : 25 * mm});
        }
    });
